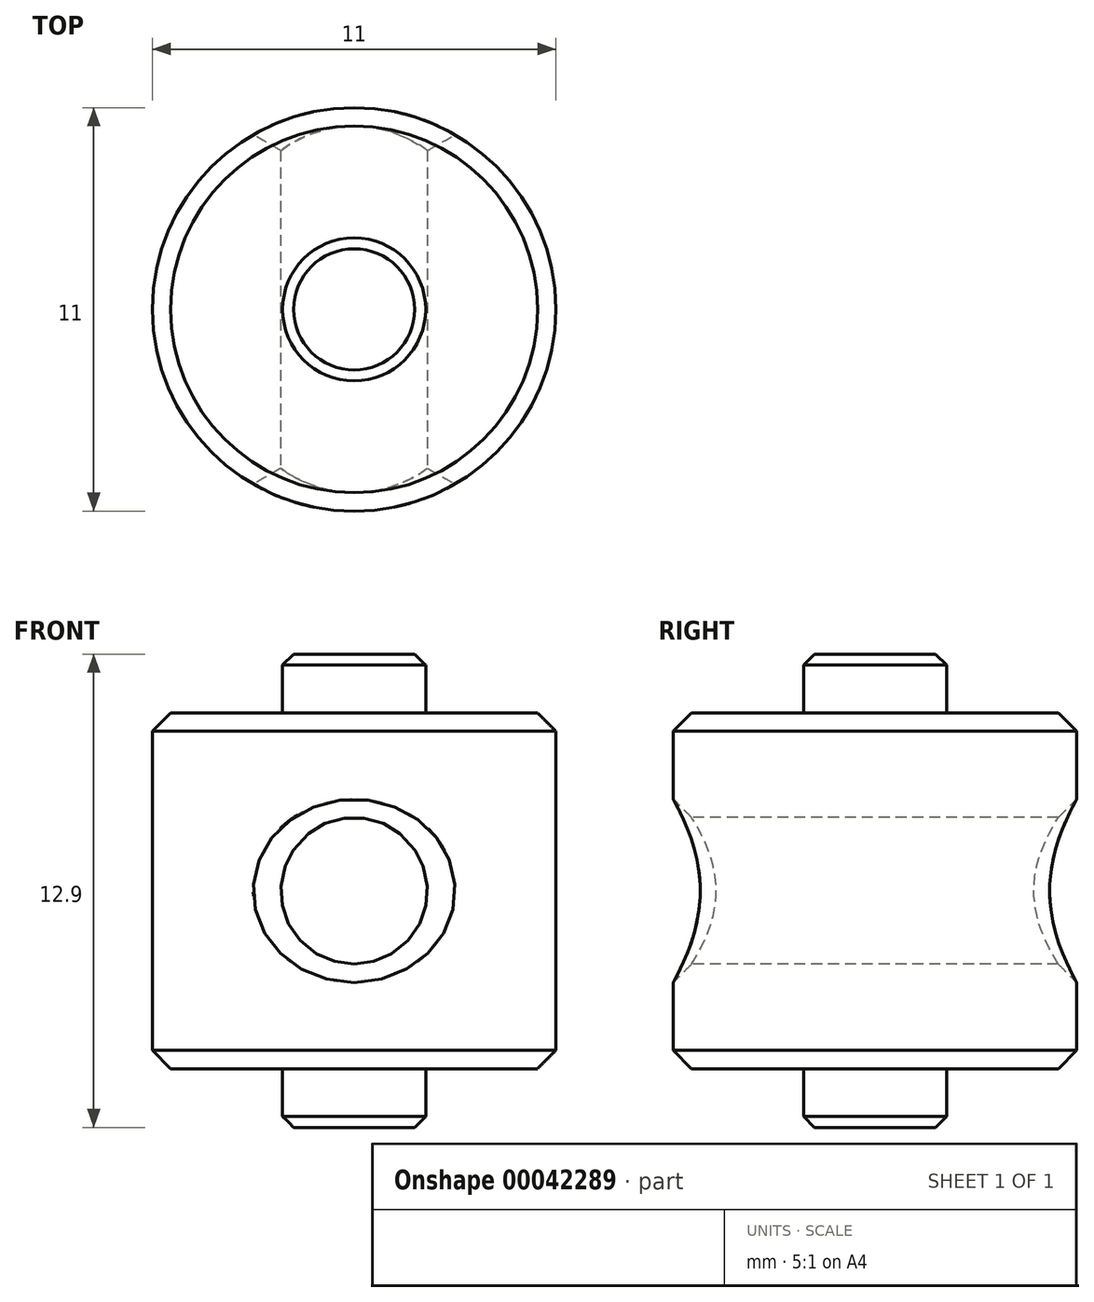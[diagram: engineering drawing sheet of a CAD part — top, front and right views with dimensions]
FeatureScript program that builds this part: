
annotation { "Feature Type Name" : "Feature", "Feature Type Description" : "" }
export const myFeature = defineFeature(function(context is Context, id is Id, definition is map)
    precondition{}
    {
        {
            var Q0;
            Q0=qCreatedBy(makeId("Top.planeOp"),FACE);
            var sketch = newSketch(context, id + "F0", { "sketchPlane" : qUnion([Q0])});
            skCircle(sketch, "E0", {"center": v(0, 0) * mm, "radius": 5.5 * mm});
            skSolve(sketch);
        }
        {
            var Q0;
            Q0 = qSketchRegion(id + "F0", true);
            extrude(context, id + "F1", {"entities" : qUnion([Q0]), "depth" : 9.7 * mm, "symmetric" : true});
        }
        {
            var Q0;
            Q0=makeQuery(id+"F1.opExtrude","CAP_FACE",FACE,{"disambiguationData":[OSD([sQuery(id+"F0.wireOp",EDGE,"E0")])],"isStart":false});
            var sketch = newSketch(context, id + "F2", { "sketchPlane" : qUnion([Q0])});
            skCircle(sketch, "E1", {"center": v(0, 0) * mm, "radius": 1.95 * mm});
            skSolve(sketch);
        }
        {
            var Q0;
            Q0 = qSketchRegion(id + "F2", true);
            extrude(context, id + "F3", {"entities" : qUnion([Q0]), "depth" : 1.6 * mm});
        }
        {
            var Q0;
            Q0=makeQuery(id+"F3.opExtrude","SWEPT_BODY",BODY,{"disambiguationData":[OSD([sQuery(id+"F2.wireOp",EDGE,"E1")])]});
            var Q1;
            Q1=qCreatedBy(makeId("Top.planeOp"),FACE);
            mirror(context, id + "F4", {"operationType" : NewBodyOperationType.ADD, "entities" : qUnion([Q0]), "mirrorPlane" : qUnion([Q1])});
        }
        {
            var Q0;
            Q0=qCreatedBy(makeId("Front.planeOp"),FACE);
            var sketch = newSketch(context, id + "F5", { "sketchPlane" : qUnion([Q0])});
            skCircle(sketch, "E2", {"center": v(0, 0) * mm, "radius": 2 * mm});
            skSolve(sketch);
        }
        {
            var Q0;
            Q0 = qSketchRegion(id + "F5", true);
            extrude(context, id + "F6", {"entities" : qUnion([Q0]), "operationType" : NewBodyOperationType.REMOVE, "oppositeDirection" : true, "depth" : 25 * mm, "symmetric" : true});
        }
        {
            var Q0;
            Q0=makeQuery(id+"F1.opExtrude","CAP_EDGE",EDGE,{"disambiguationData":[OSD([sQuery(id+"F0.wireOp",EDGE,"E0")])],"isStart":true});
            var Q1;
            Q1=makeQuery(id+"F1.opExtrude","CAP_EDGE",EDGE,{"disambiguationData":[OSD([sQuery(id+"F0.wireOp",EDGE,"E0")])],"isStart":false});
            chamfer(context, id + "F7", {"entities" : qUnion([Q0, Q1]), "width" : 0.5 * mm, "tangentPropagation" : true});
        }
        {
            var Q0;
            Q0=makeQuery(id+"F6.boolean.opBoolean","INTERSECT",EDGE,{"disambiguationData":[OD(0.0)],"derivedFrom":[makeQuery(id+"F1.opExtrude","SWEPT_FACE",FACE,{"disambiguationData":[OSD([sQuery(id+"F0.wireOp",EDGE,"E0")])]}),makeQuery(id+"F6.opExtrude","SWEPT_FACE",FACE,{"disambiguationData":[OSD([sQuery(id+"F5.wireOp",EDGE,"E2")])]})]});
            var Q1;
            Q1=makeQuery(id+"F6.boolean.opBoolean","INTERSECT",EDGE,{"disambiguationData":[OD(1.0)],"derivedFrom":[makeQuery(id+"F1.opExtrude","SWEPT_FACE",FACE,{"disambiguationData":[OSD([sQuery(id+"F0.wireOp",EDGE,"E0")])]}),makeQuery(id+"F6.opExtrude","SWEPT_FACE",FACE,{"disambiguationData":[OSD([sQuery(id+"F5.wireOp",EDGE,"E2")])]})]});
            chamfer(context, id + "F8", {"entities" : qUnion([Q0, Q1]), "width" : 0.5 * mm, "tangentPropagation" : true});
        }
        {
            var Q0;
            Q0=makeQuery(id+"F4.opPattern","COPY",EDGE,{"derivedFrom":makeQuery(id+"F3.opExtrude","CAP_EDGE",EDGE,{"disambiguationData":[OSD([sQuery(id+"F2.wireOp",EDGE,"E1")])],"isStart":false}),"instanceName":"1"});
            var Q1;
            Q1=makeQuery(id+"F3.opExtrude","CAP_EDGE",EDGE,{"disambiguationData":[OSD([sQuery(id+"F2.wireOp",EDGE,"E1")])],"isStart":false});
            chamfer(context, id + "F9", {"entities" : qUnion([Q0, Q1]), "width" : 0.3 * mm, "tangentPropagation" : true});
        }
    });
